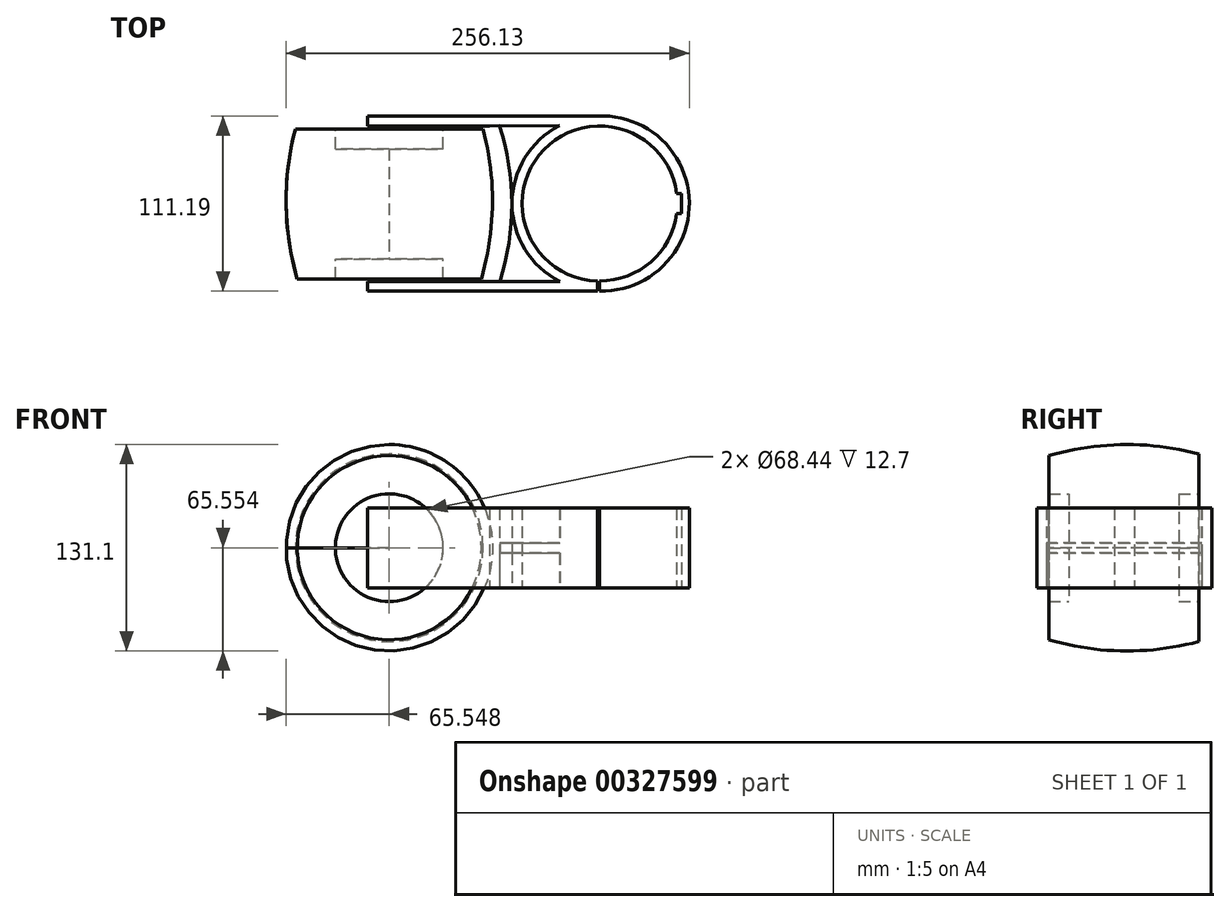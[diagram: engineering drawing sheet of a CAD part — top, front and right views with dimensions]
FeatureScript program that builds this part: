
annotation { "Feature Type Name" : "Feature", "Feature Type Description" : "" }
export const myFeature = defineFeature(function(context is Context, id is Id, definition is map)
    precondition{}
    {
        {
            var Q0;
            Q0=qCreatedBy(makeId("Top.planeOp"),FACE);
            var sketch = newSketch(context, id + "F0", { "sketchPlane" : qUnion([Q0])});
            skArc(sketch, "E0", {"start": v(0, -49.21) * mm, "mid": v(0.63, 49.2) * mm, "end": v(-1.27, -49.2) * mm});
            skArc(sketch, "E1.0", {"start": v(-25.41, 49.4) * mm, "mid": v(-55.56, -0.1) * mm, "end": v(-25.23, -49.5) * mm});
            skLineSegment(sketch, "E2", {"start": v(-1.27, 55.55) * mm, "end": v(-1.27, 49.2) * mm});
            skLineSegment(sketch, "E3", {"start": v(0, -49.21) * mm, "end": v(0, -55.56) * mm});
            skLineSegment(sketch, "E4.bottom", {"start": v(-1.27, 55.55) * mm, "end": v(-147.32, 55.55) * mm});
            skLineSegment(sketch, "E4.top", {"start": v(-1.27, -55.58) * mm, "end": v(-147.32, -55.58) * mm});
            skLineSegment(sketch, "E5.trimOffspring", {"start": v(-1.27, -49.2) * mm, "end": v(-1.27, -55.58) * mm});
            skLineSegment(sketch, "E6", {"start": v(-147.32, 55.55) * mm, "end": v(-147.32, 49.1) * mm});
            skLineSegment(sketch, "E7", {"start": v(-147.32, -55.58) * mm, "end": v(-147.32, -49.5) * mm});
            skLineSegment(sketch, "E8", {"start": v(-147.32, -49.5) * mm, "end": v(-25.23, -49.5) * mm});
            skArc(sketch, "E9", {"start": v(-193.14, 47.34) * mm, "mid": v(-199.06, -0.36) * mm, "end": v(-191.98, -47.9) * mm});
            skLineSegment(sketch, "E10", {"start": v(-167.74, -47.9) * mm, "end": v(-167.74, -35.2) * mm});
            skLineSegment(sketch, "E11", {"start": v(-167.74, -35.2) * mm, "end": v(-161.4, -35.2) * mm});
            skLineSegment(sketch, "E12", {"start": v(-161.4, -35.2) * mm, "end": v(-161.4, 34.64) * mm});
            skLineSegment(sketch, "E13", {"start": v(-161.4, 34.64) * mm, "end": v(-167.74, 34.64) * mm});
            skLineSegment(sketch, "E14", {"start": v(-167.74, 34.64) * mm, "end": v(-167.74, 47.34) * mm});
            skLineSegment(sketch, "E15", {"start": v(-193.14, 47.34) * mm, "end": v(-167.74, 47.34) * mm});
            skLineSegment(sketch, "E16", {"start": v(-191.98, -47.9) * mm, "end": v(-167.74, -47.9) * mm});
            skLineSegment(sketch, "E17", {"start": v(-161.4, 34.64) * mm, "end": v(-133.52, 34.64) * mm});
            skLineSegment(sketch, "E18", {"start": v(-161.4, -35.2) * mm, "end": v(-133.52, -35.2) * mm});
            skLineSegment(sketch, "E19", {"start": v(-133.52, 34.64) * mm, "end": v(-133.52, -35.2) * mm});
            skLineSegment(sketch, "E20", {"start": v(-147.32, 49.1) * mm, "end": v(-25.41, 49.4) * mm});
            skLineSegment(sketch, "E21", {"start": v(-63.51, 49.4) * mm, "end": v(-69.86, 49.3) * mm});
            skLineSegment(sketch, "E22", {"start": v(-63.33, -49.5) * mm, "end": v(-69.68, -49.5) * mm});
            skArc(sketch, "E23", {"start": v(-69.68, -49.5) * mm, "mid": v(-61.43, -0.09) * mm, "end": v(-69.86, 49.3) * mm});
            skArc(sketch, "E24", {"start": v(-63.33, -49.5) * mm, "mid": v(-55.7, -0.03) * mm, "end": v(-63.51, 49.4) * mm});
            skLineSegment(sketch, "E25", {"start": v(-69.68, -49.5) * mm, "end": v(-63.33, -49.5) * mm});
            skLineSegment(sketch, "E26", {"start": v(-69.86, 49.3) * mm, "end": v(-63.51, 49.4) * mm});
            skArc(sketch, "E27", {"start": v(0, -55.56) * mm, "mid": v(57.05, 0.65) * mm, "end": v(-1.27, 55.55) * mm});
            skArc(sketch, "E28", {"start": v(0, -49.21) * mm, "mid": v(49.45, 0.64) * mm, "end": v(-1.27, 49.2) * mm});
            skLineSegment(sketch, "E29", {"start": v(49.04, 6.35) * mm, "end": v(52.21, 6.35) * mm});
            skLineSegment(sketch, "E30", {"start": v(52.21, 6.35) * mm, "end": v(52.21, -6.35) * mm});
            skLineSegment(sketch, "E31", {"start": v(52.21, -6.35) * mm, "end": v(49.04, -6.35) * mm});
            skSolve(sketch);
        }
        {
            var Q0;
            {var subQ3=sQuery(id+"F0.wireOp",EDGE,"E4.bottom");Q0=makeQuery(id+"F0.imprint","IMPRINT",FACE,{"disambiguationData":[TD([[makeQuery(id+"F0.imprint","IMPRINT",EDGE,{"derivedFrom":subQ3}),1.0]])]});}
            var Q1;
            {var subQ2=sQuery(id+"F0.wireOp",EDGE,"E4.top");Q1=makeQuery(id+"F0.imprint","IMPRINT",FACE,{"disambiguationData":[TD([[makeQuery(id+"F0.imprint","IMPRINT",EDGE,{"derivedFrom":subQ2}),-1.0]])]});}
            var Q2;
            {var subQ4=sQuery(id+"F0.wireOp",EDGE,"E2");Q2=makeQuery(id+"F0.imprint","IMPRINT",FACE,{"disambiguationData":[TD([[makeQuery(id+"F0.imprint","IMPRINT",EDGE,{"derivedFrom":subQ4}),-1.0]])]});}
            extrude(context, id + "F1", {"entities" : qUnion([Q0, Q1, Q2]), "endBound" : BoundingType.SYMMETRIC, "depth" : 50.8 * mm});
        }
        {
            var Q0;
            Q0=makeQuery(id+"F0.imprint","IMPRINT",FACE,{"disambiguationData":[TD([[makeQuery(id+"F0.imprint","IMPRINT",EDGE,{"derivedFrom":sQuery(id+"F0.wireOp",EDGE,"E9")}),1.0]])]});
            extrude(context, id + "F2", {"entities" : qUnion([Q0]), "depth" : 0.25 * mm});
        }
        {
            var Q0;
            Q0=makeQuery(id+"F0.imprint","IMPRINT",FACE,{"disambiguationData":[TD([[makeQuery(id+"F0.imprint","IMPRINT",EDGE,{"derivedFrom":sQuery(id+"F0.wireOp",EDGE,"E12")}),-1.0]])]});
            extrude(context, id + "F3", {"entities" : qUnion([Q0]), "operationType" : NewBodyOperationType.ADD, "depth" : 0.25 * mm});
        }
        {
            var Q0;
            Q0=makeQuery(id+"F2.opExtrude","CAP_FACE",FACE,{"disambiguationData":[OSD([sQuery(id+"F0.wireOp",EDGE,"E9"),sQuery(id+"F0.wireOp",EDGE,"E10"),sQuery(id+"F0.wireOp",EDGE,"E11"),sQuery(id+"F0.wireOp",EDGE,"E12"),sQuery(id+"F0.wireOp",EDGE,"E13"),sQuery(id+"F0.wireOp",EDGE,"E14"),sQuery(id+"F0.wireOp",EDGE,"E15"),sQuery(id+"F0.wireOp",EDGE,"E16")])],"isStart":false});
            var Q1;
            Q1=makeQuery(id+"F3.opExtrude","CAP_EDGE",EDGE,{"disambiguationData":[OSD([sQuery(id+"F0.wireOp",EDGE,"E19")])],"isStart":false});
            revolve(context, id + "F4", {"entities" : qUnion([Q0]), "axis" : qUnion([Q1]), "revolveType" : RevolveType.FULL});
        }
        {
            var Q0;
            {var subQ1=sQuery(id+"F0.wireOp",EDGE,"U8nKFDl3-79kX-OwHk-EaO0-BTTa4R9wu8cM");var subQ2=sQuery(id+"F0.wireOp",EDGE,"E1.0");var subQ4=makeQuery(id+"F0.imprint","INTERSECT",VERTEX,{"derivedFrom":[subQ2,subQ1]});Q0=makeQuery(id+"F0.imprint","IMPRINT",FACE,{"disambiguationData":[TD([[makeQuery(id+"F0.imprint","IMPRINT",EDGE,{"disambiguationData":[TD([[subQ4,1.0]])],"derivedFrom":subQ2}),-1.0]])]});}
            var Q1;
            {var subQ0=sQuery(id+"F0.wireOp",EDGE,"Sarp5LDe-epc4-feCA-tBnT-7ws2dZc43zB3");var subQ3=sQuery(id+"F0.wireOp",EDGE,"E24");var subQ5=makeQuery(id+"F0.imprint","INTERSECT",VERTEX,{"derivedFrom":[subQ0,subQ3]});Q1=makeQuery(id+"F0.imprint","IMPRINT",FACE,{"disambiguationData":[TD([[makeQuery(id+"F0.imprint","IMPRINT",EDGE,{"disambiguationData":[TD([[subQ5,-1.0]])],"derivedFrom":subQ0}),-1.0]])]});}
            var Q2;
            Q2=sQuery(id+"F0.wireOp",EDGE,"E25");
            var Q3;
            Q3=sQuery(id+"F0.wireOp",EDGE,"E24");
            var Q4;
            Q4=sQuery(id+"F0.wireOp",EDGE,"E23");
            var Q5;
            Q5=sQuery(id+"F0.wireOp",EDGE,"E21");
            extrude(context, id + "F5", {"entities" : qUnion([Q0, Q1]), "operationType" : NewBodyOperationType.ADD, "surfaceEntities" : qUnion([Q2, Q3, Q4, Q5]), "endBound" : BoundingType.SYMMETRIC, "depth" : 6.35 * mm});
        }
        {
            var Q0;
            Q0=makeQuery(id+"F0.imprint","IMPRINT",FACE,{"disambiguationData":[TD([[makeQuery(id+"F0.imprint","IMPRINT",EDGE,{"derivedFrom":sQuery(id+"F0.wireOp",EDGE,"E27")}),1.0]])]});
            extrude(context, id + "F6", {"entities" : qUnion([Q0]), "operationType" : NewBodyOperationType.ADD, "endBound" : BoundingType.SYMMETRIC, "depth" : 50.8 * mm});
        }
        {
            var Q0;
            Q0=sQuery(id+"F0.wireOp",EDGE,"E31");
            var Q1;
            Q1=sQuery(id+"F0.wireOp",EDGE,"E29");
            var Q2;
            Q2=sQuery(id+"F0.wireOp",EDGE,"E30");
            extrude(context, id + "F7", {"bodyType" : ToolBodyType.SURFACE, "surfaceEntities" : qUnion([Q0, Q1, Q2]), "depth" : 25.4 * mm});
        }
    });
